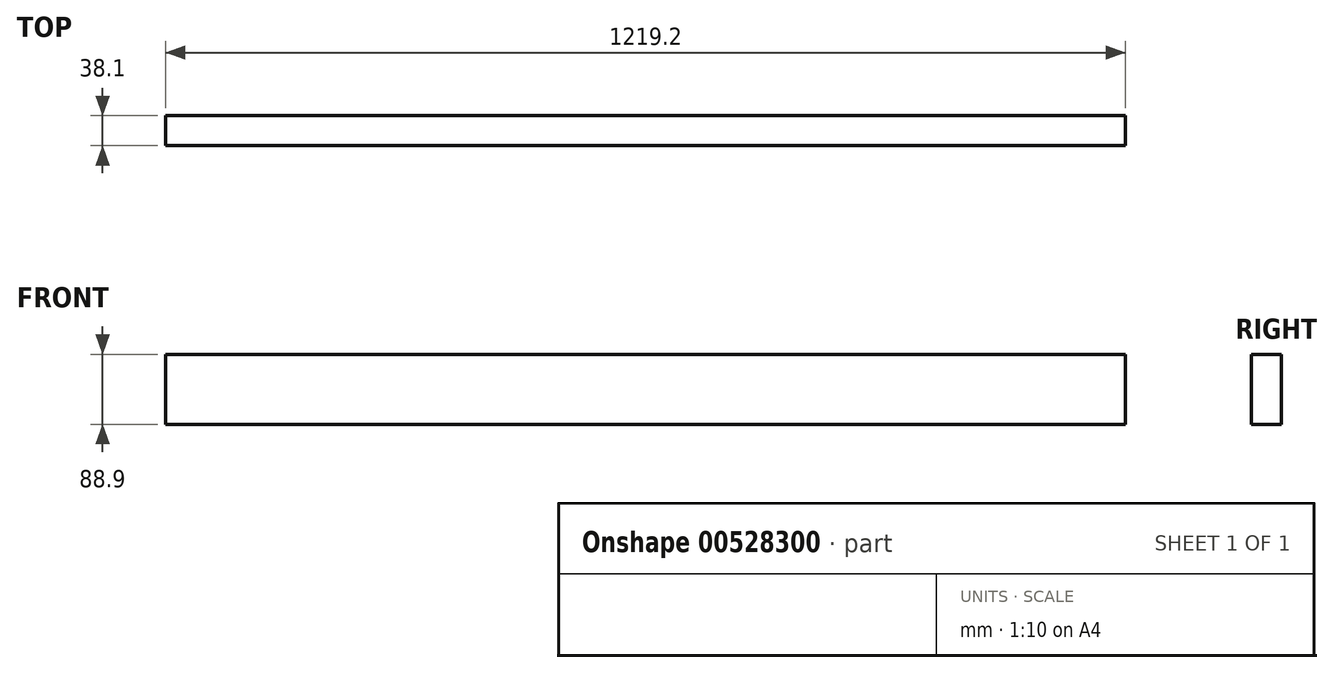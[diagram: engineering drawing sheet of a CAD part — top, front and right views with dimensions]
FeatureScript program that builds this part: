
annotation { "Feature Type Name" : "Feature", "Feature Type Description" : "" }
export const myFeature = defineFeature(function(context is Context, id is Id, definition is map)
    precondition{}
    {
        {
            var Q0;
            Q0=qCreatedBy(makeId("Top.planeOp"),FACE);
            var sketch = newSketch(context, id + "F0", { "sketchPlane" : qUnion([Q0])});
            skLineSegment(sketch, "E0.bottom", {"start": v(609.6, -19.05) * mm, "end": v(-609.6, -19.05) * mm});
            skLineSegment(sketch, "E0.top", {"start": v(609.6, 19.05) * mm, "end": v(-609.6, 19.05) * mm});
            skLineSegment(sketch, "E0.left", {"start": v(609.6, -19.05) * mm, "end": v(609.6, 19.05) * mm});
            skLineSegment(sketch, "E0.right", {"start": v(-609.6, -19.05) * mm, "end": v(-609.6, 19.05) * mm});
            skPoint(sketch, "E0.middle", {"position": v(0, 0) * mm});
            skSolve(sketch);
        }
        {
            var Q0;
            Q0=makeQuery(id+"F0.imprint","IMPRINT",FACE,{"disambiguationData":[TD([[makeQuery(id+"F0.imprint","IMPRINT",EDGE,{"derivedFrom":sQuery(id+"F0.wireOp",EDGE,"E0.bottom")}),-1.0]])]});
            extrude(context, id + "F1", {"entities" : qUnion([Q0]), "depth" : 88.9 * mm, "offsetDistance" : 25.4 * mm});
        }
    });
